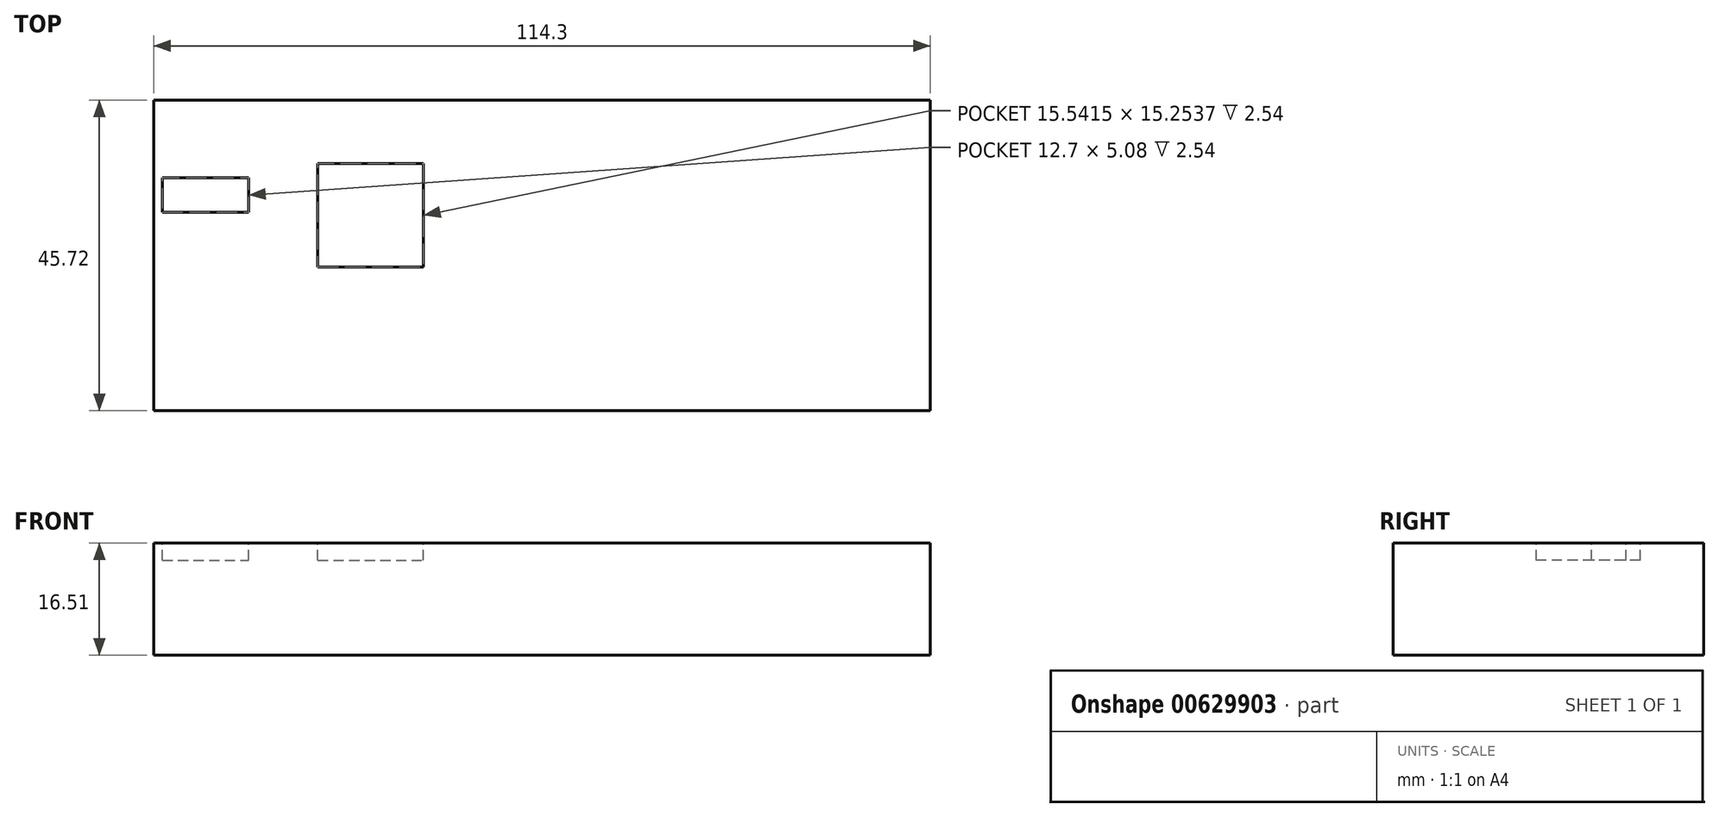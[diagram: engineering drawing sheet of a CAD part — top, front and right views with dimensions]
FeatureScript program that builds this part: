
annotation { "Feature Type Name" : "Feature", "Feature Type Description" : "" }
export const myFeature = defineFeature(function(context is Context, id is Id, definition is map)
    precondition{}
    {
        {
            var Q0;
            Q0=qCreatedBy(makeId("Top.planeOp"),FACE);
            var sketch = newSketch(context, id + "F0", { "sketchPlane" : qUnion([Q0])});
            skLineSegment(sketch, "E0.bottom", {"start": v(-27.2, 17.54) * mm, "end": v(87.1, 17.54) * mm});
            skLineSegment(sketch, "E0.top", {"start": v(-27.2, -28.18) * mm, "end": v(87.1, -28.18) * mm});
            skLineSegment(sketch, "E0.left", {"start": v(-27.2, 17.54) * mm, "end": v(-27.2, -28.18) * mm});
            skLineSegment(sketch, "E0.right", {"start": v(87.1, 17.54) * mm, "end": v(87.1, -28.18) * mm});
            skSolve(sketch);
        }
        {
            var Q0;
            Q0=makeQuery(id+"F0.imprint","IMPRINT",FACE,{"disambiguationData":[TD([[makeQuery(id+"F0.imprint","IMPRINT",EDGE,{"derivedFrom":sQuery(id+"F0.wireOp",EDGE,"E0.bottom")}),-1.0]])]});
            extrude(context, id + "F1", {"entities" : qUnion([Q0]), "depth" : 16.5 * mm, "offsetDistance" : 25.4 * mm});
        }
        {
            var Q0;
            Q0=makeQuery(id+"F1.opExtrude","CAP_FACE",FACE,{"disambiguationData":[OSD([sQuery(id+"F0.wireOp",EDGE,"E0.bottom"),sQuery(id+"F0.wireOp",EDGE,"E0.top"),sQuery(id+"F0.wireOp",EDGE,"E0.left"),sQuery(id+"F0.wireOp",EDGE,"E0.right")])],"isStart":false});
            var sketch = newSketch(context, id + "F2", { "sketchPlane" : qUnion([Q0])});
            skLineSegment(sketch, "E1.bottom", {"start": v(-25.94, 6.1) * mm, "end": v(-13.24, 6.1) * mm});
            skLineSegment(sketch, "E1.top", {"start": v(-25.94, 1.03) * mm, "end": v(-13.24, 1.03) * mm});
            skLineSegment(sketch, "E1.left", {"start": v(-25.94, 6.1) * mm, "end": v(-25.94, 1.03) * mm});
            skLineSegment(sketch, "E1.right", {"start": v(-13.24, 6.1) * mm, "end": v(-13.24, 1.03) * mm});
            skLineSegment(sketch, "E2.bottom", {"start": v(-3.04, 8.2) * mm, "end": v(12.5, 8.2) * mm});
            skLineSegment(sketch, "E2.top", {"start": v(-3.04, -7.05) * mm, "end": v(12.5, -7.05) * mm});
            skLineSegment(sketch, "E2.left", {"start": v(-3.04, 8.2) * mm, "end": v(-3.04, -7.05) * mm});
            skLineSegment(sketch, "E2.right", {"start": v(12.5, 8.2) * mm, "end": v(12.5, -7.05) * mm});
            skSolve(sketch);
        }
        {
            var Q0;
            Q0=makeQuery(id+"F2.imprint","IMPRINT",FACE,{"disambiguationData":[TD([[makeQuery(id+"F2.imprint","IMPRINT",EDGE,{"derivedFrom":sQuery(id+"F2.wireOp",EDGE,"E1.bottom")}),-1.0]])]});
            var Q1;
            Q1=makeQuery(id+"F2.imprint","IMPRINT",FACE,{"disambiguationData":[TD([[makeQuery(id+"F2.imprint","IMPRINT",EDGE,{"derivedFrom":sQuery(id+"F2.wireOp",EDGE,"E2.bottom")}),-1.0]])]});
            extrude(context, id + "F3", {"entities" : qUnion([Q0, Q1]), "operationType" : NewBodyOperationType.REMOVE, "oppositeDirection" : true, "depth" : 2.54 * mm, "offsetDistance" : 25.4 * mm});
        }
    });
